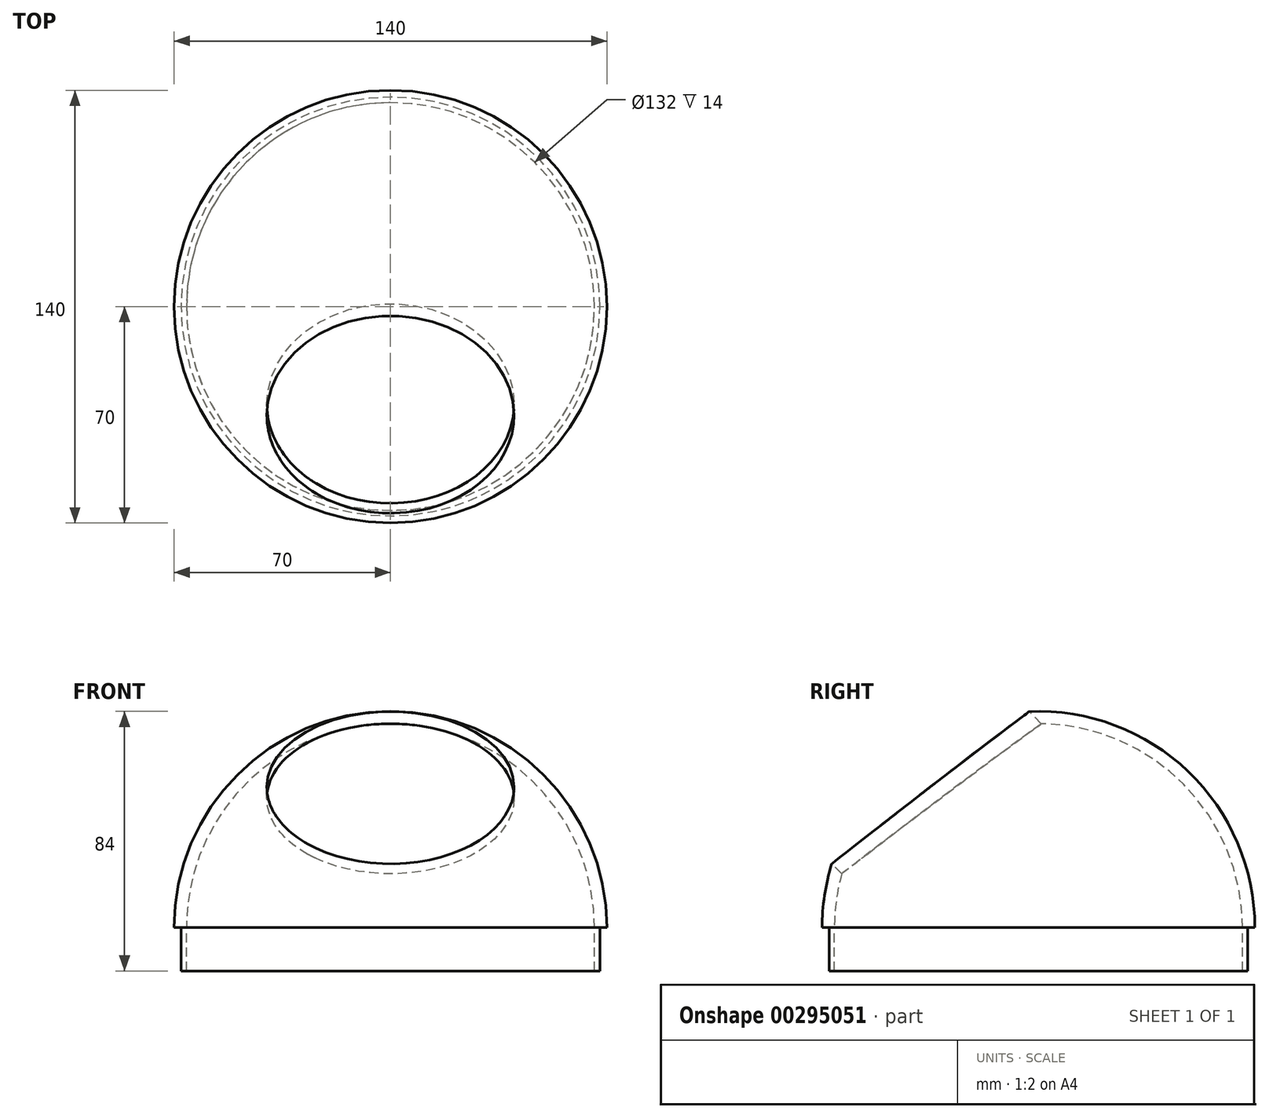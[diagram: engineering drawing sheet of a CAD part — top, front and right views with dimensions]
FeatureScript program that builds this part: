
annotation { "Feature Type Name" : "Feature", "Feature Type Description" : "" }
export const myFeature = defineFeature(function(context is Context, id is Id, definition is map)
    precondition{}
    {
        {
            var Q0;
            Q0=qCreatedBy(makeId("Top.planeOp"),FACE);
            var sketch = newSketch(context, id + "F0", { "sketchPlane" : qUnion([Q0])});
            skArc(sketch, "E0", {"start": v(70, 0) * mm, "mid": v(0, 70) * mm, "end": v(-70, 0) * mm});
            skLineSegment(sketch, "E1", {"start": v(-70, 0) * mm, "end": v(70, 0) * mm});
            skSolve(sketch);
        }
        {
            var Q0;
            Q0 = qSketchRegion(id + "F0", true);
            var Q1;
            Q1=sQuery(id+"F0.wireOp",EDGE,"E1");
            revolve(context, id + "F1", {"entities" : qUnion([Q0]), "axis" : qUnion([Q1]), "revolveType" : RevolveType.ONE_DIRECTION, "angle" : 180 * degree});
        }
        {
            var Q0;
            Q0=makeQuery(id+"F1.opRevolve","CAP_FACE",FACE,{"disambiguationData":[OSD([sQuery(id+"F0.wireOp",EDGE,"E0"),sQuery(id+"F0.wireOp",EDGE,"E1")])],"isStart":true});
            shell(context, id + "F2", {"entities" : qUnion([Q0]), "thickness" : 4 * mm});
        }
        {
            var Q0;
            Q0=qCreatedBy(makeId("Right.planeOp"),FACE);
            var sketch = newSketch(context, id + "F3", { "sketchPlane" : qUnion([Q0])});
            skLineSegment(sketch, "E2", {"start": v(-75, 0) * mm, "end": v(-75, 50) * mm, "construction": true});
            skLineSegment(sketch, "E3", {"start": v(-75, 50) * mm, "end": v(-39.64, 85.36) * mm});
            skLineSegment(sketch, "E4", {"start": v(-75, 50) * mm, "end": v(-74.3, 49.3) * mm});
            skLineSegment(sketch, "E5", {"start": v(-74.3, 49.3) * mm, "end": v(-38.94, 84.65) * mm});
            skLineSegment(sketch, "E6", {"start": v(-38.94, 84.65) * mm, "end": v(-39.64, 85.36) * mm});
            skSolve(sketch);
        }
        {
            var Q0;
            Q0 = qSketchRegion(id + "F3", true);
            extrude(context, id + "F4", {"entities" : qUnion([Q0]), "depth" : 25 * mm, "hasSecondDirection" : true, "secondDirectionOppositeDirection" : true, "secondDirectionDepth" : 25 * mm});
        }
        {
            var Q0;
            Q0=makeQuery(id+"F4.opExtrude","SWEPT_FACE",FACE,{"disambiguationData":[OSD([sQuery(id+"F3.wireOp",EDGE,"E3")])]});
            var sketch = newSketch(context, id + "F5", { "sketchPlane" : qUnion([Q0])});
            skCircle(sketch, "E7", {"center": v(0, 7.32) * mm, "radius": 40 * mm});
            skPoint(sketch, "E7.centerSnap0", {"position": v(25, 7.32) * mm});
            skPoint(sketch, "E7.centerSnap1", {"position": v(0, 32.32) * mm});
            skSolve(sketch);
        }
        {
            var Q0;
            Q0 = qSketchRegion(id + "F5", true);
            extrude(context, id + "F6", {"entities" : qUnion([Q0]), "operationType" : NewBodyOperationType.REMOVE, "oppositeDirection" : true, "depth" : 50 * mm});
        }
        {
            var Q0;
            Q0=makeQuery(id+"F1.opRevolve","CAP_FACE",FACE,{"disambiguationData":[OSD([sQuery(id+"F0.wireOp",EDGE,"E0"),sQuery(id+"F0.wireOp",EDGE,"E1")])],"isStart":true});
            var sketch = newSketch(context, id + "F7", { "sketchPlane" : qUnion([Q0])});
            skCircle(sketch, "E8", {"center": v(0, 0) * mm, "radius": 67.75 * mm});
            skCircle(sketch, "E9", {"center": v(0, 0) * mm, "radius": 66 * mm});
            skSolve(sketch);
        }
        {
            var Q0;
            Q0 = qSketchRegion(id + "F7", true);
            extrude(context, id + "F8", {"entities" : qUnion([Q0]), "operationType" : NewBodyOperationType.ADD, "depth" : 14 * mm});
        }
    });
